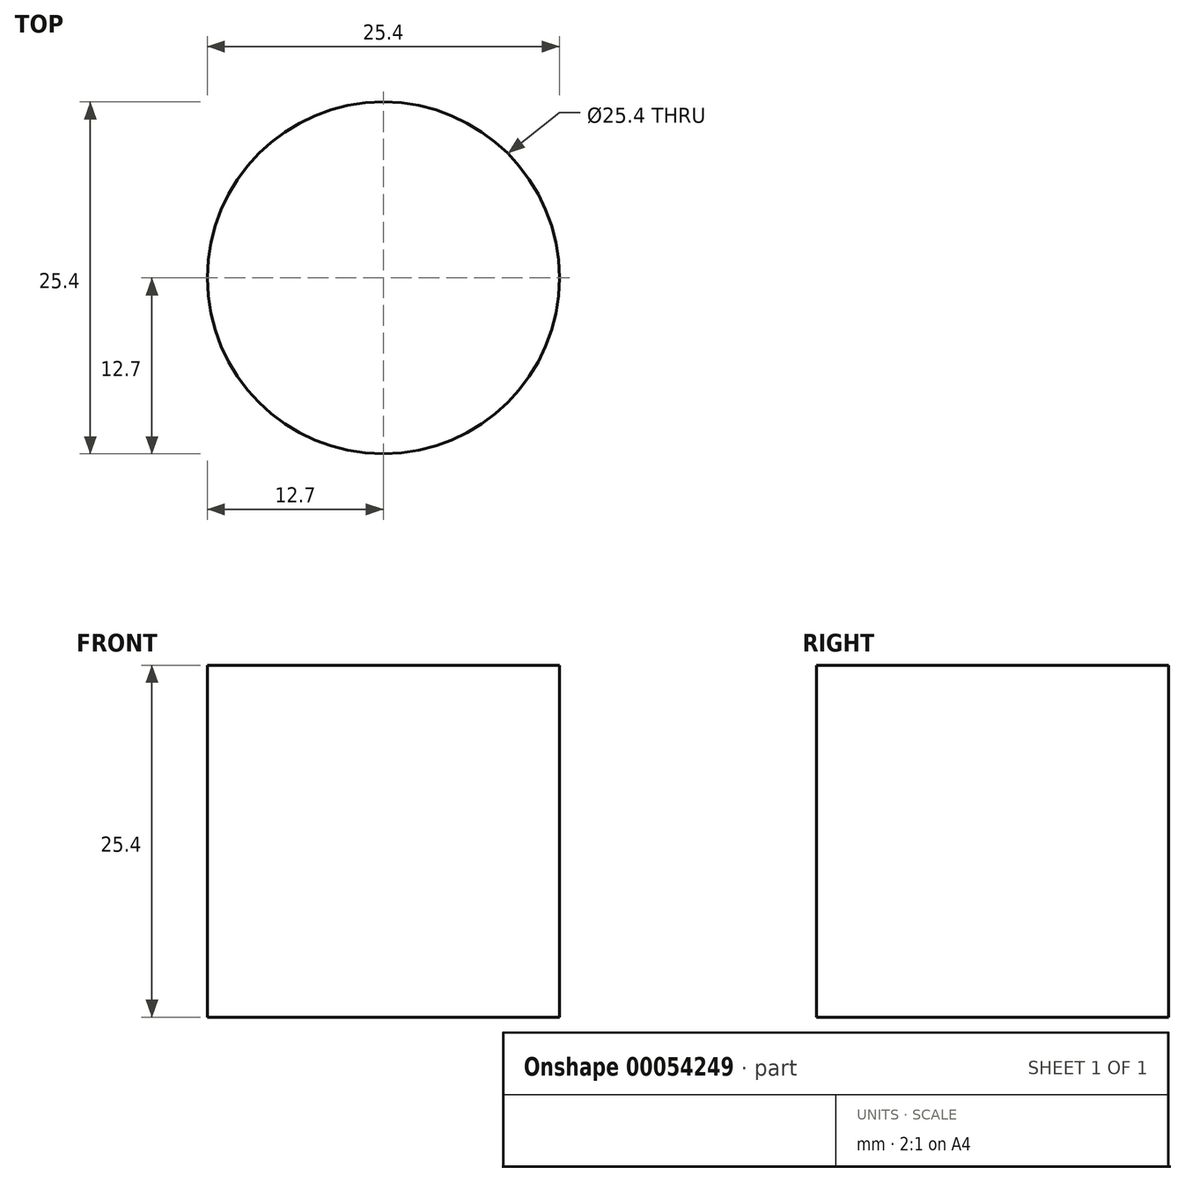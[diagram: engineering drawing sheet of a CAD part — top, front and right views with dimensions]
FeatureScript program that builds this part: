
annotation { "Feature Type Name" : "Feature", "Feature Type Description" : "" }
export const myFeature = defineFeature(function(context is Context, id is Id, definition is map)
    precondition{}
    {
        {
            var Q0;
            Q0=qCreatedBy(makeId("Top.planeOp"),FACE);
            var sketch = newSketch(context, id + "F0", { "sketchPlane" : qUnion([Q0])});
            skCircle(sketch, "E0", {"center": v(0, 0) * mm, "radius": 12.7 * mm});
            skCircle(sketch, "E1", {"center": v(0, 0) * mm, "radius": 19.05 * mm});
            skSolve(sketch);
        }
        {
            var Q0;
            Q0=sQuery(id+"F0.wireOp",EDGE,"E0");
            extrude(context, id + "F1", {"bodyType" : ToolBodyType.SURFACE, "surfaceEntities" : qUnion([Q0]), "oppositeDirection" : true, "depth" : 25.4 * mm});
        }
    });
